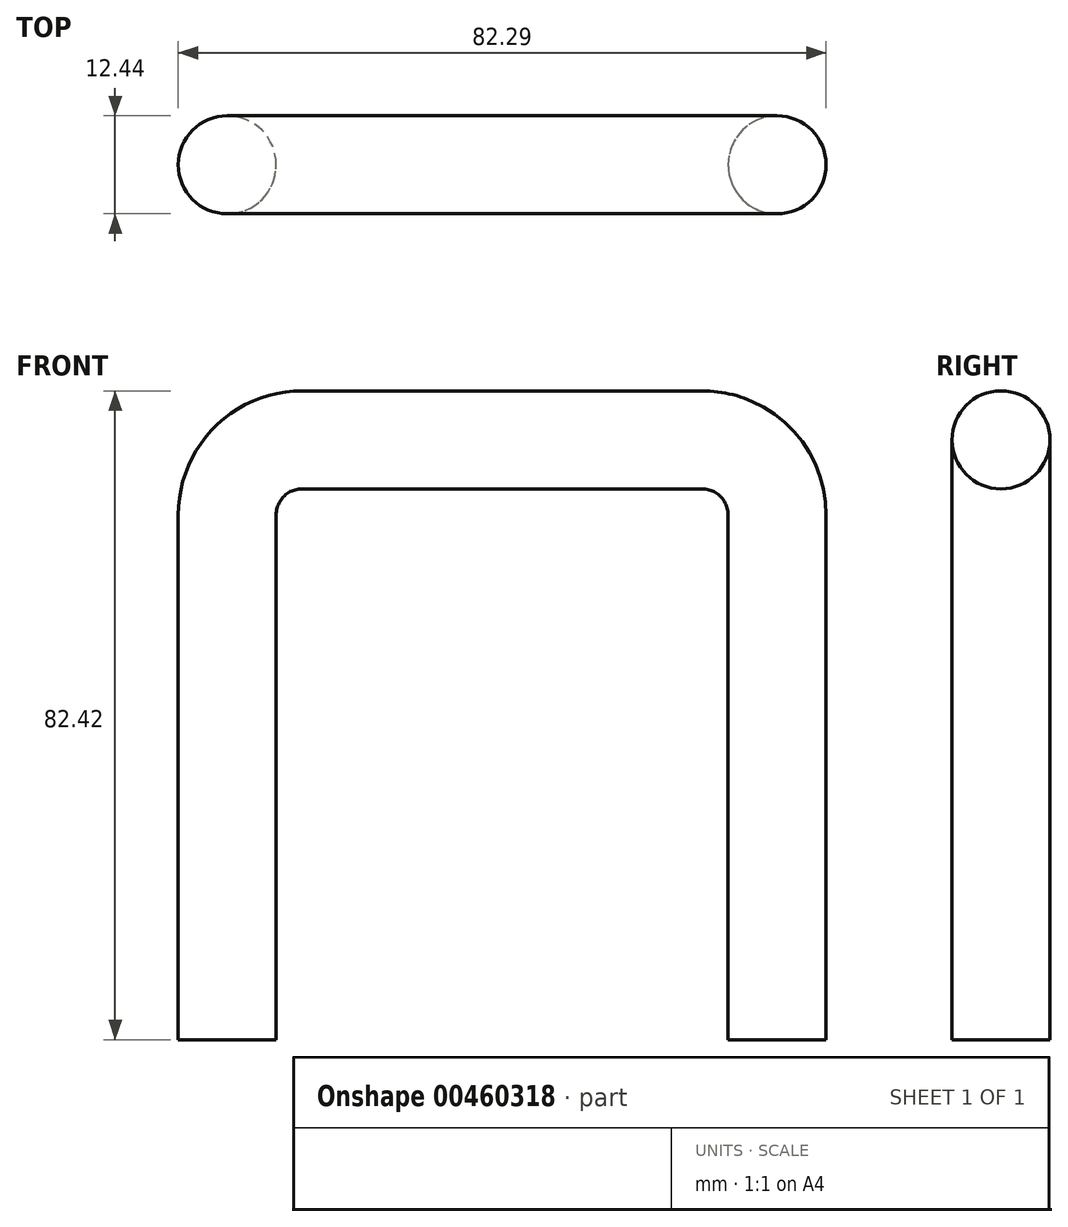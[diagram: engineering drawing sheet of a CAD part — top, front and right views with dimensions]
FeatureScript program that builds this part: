
annotation { "Feature Type Name" : "Feature", "Feature Type Description" : "" }
export const myFeature = defineFeature(function(context is Context, id is Id, definition is map)
    precondition{}
    {
        {
            var Q0;
            Q0=qCreatedBy(makeId("Top.planeOp"),FACE);
            var sketch = newSketch(context, id + "F0", { "sketchPlane" : qUnion([Q0])});
            skCircle(sketch, "E0", {"center": v(0, 0) * mm, "radius": 6.22 * mm});
            skSolve(sketch);
        }
        {
            var Q0;
            Q0=qCreatedBy(makeId("Front.planeOp"),FACE);
            var sketch = newSketch(context, id + "F1", { "sketchPlane" : qUnion([Q0])});
            skLineSegment(sketch, "E1", {"start": v(0, 0) * mm, "end": v(0, 66.67) * mm});
            skLineSegment(sketch, "E2", {"start": v(9.52, 76.2) * mm, "end": v(60.32, 76.2) * mm});
            skLineSegment(sketch, "E3", {"start": v(69.85, 66.67) * mm, "end": v(69.85, 0) * mm});
            skPoint(sketch, "E4.visualSharp", {"position": v(0, 76.2) * mm});
            skArc(sketch, "E4.filletArc", {"start": v(9.52, 76.2) * mm, "mid": v(2.79, 73.41) * mm, "end": v(0, 66.67) * mm});
            skPoint(sketch, "E5.visualSharp", {"position": v(69.85, 76.2) * mm});
            skArc(sketch, "E5.filletArc", {"start": v(69.85, 66.67) * mm, "mid": v(67.06, 73.41) * mm, "end": v(60.32, 76.2) * mm});
            skSolve(sketch);
        }
        {
            var Q0;
            Q0=makeQuery(id+"F0.imprint","IMPRINT",FACE,{"disambiguationData":[TD([[makeQuery(id+"F0.imprint","IMPRINT",EDGE,{"derivedFrom":sQuery(id+"F0.wireOp",EDGE,"E0")}),1.0]])]});
            var Q1;
            Q1=sQuery(id+"F1.wireOp",EDGE,"E1");
            var Q2;
            Q2=sQuery(id+"F1.wireOp",EDGE,"E4.filletArc");
            var Q3;
            Q3=sQuery(id+"F1.wireOp",EDGE,"E2");
            var Q4;
            Q4=sQuery(id+"F1.wireOp",EDGE,"E5.filletArc");
            var Q5;
            Q5=sQuery(id+"F1.wireOp",EDGE,"E3");
            sweep(context, id + "F2", {"profiles" : qUnion([Q0]), "path" : qUnion([Q1, Q2, Q3, Q4, Q5])});
        }
    });
